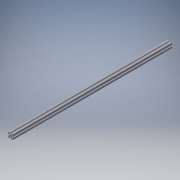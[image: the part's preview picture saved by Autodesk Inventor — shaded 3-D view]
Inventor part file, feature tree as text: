
AUTODESK INVENTOR PART (.ipt)
format: ipt  version: 2016 SP1 (Build 200210100, 210)  size: 228,352 bytes
history: native  units: mm (DEFAULTED — no unit token found)
features: other x5, extrude x1, sketch x1
ambient origin geometry x8: Origin, YZ Plane, XZ Plane, XY Plane, X Axis, Y Axis, Z Axis, Center Point
bodies: Solid1 (feature_tree)
feature tree (7):
  other  "Table"
  other  "30x30-01"
  other  "30x30-02"
  other  "30x30-03"
  other  "30x30-04"
  extrude  "Extrusion1"  [1 undecoded]
  sketch  "Sketch1"  dims[d3=0.0mm]
note: 1 required parameter value undecoded (feature->parameter linkage not recoverable at this tier; creation-order binding heuristic only, values carry confidence <= 0.55)
